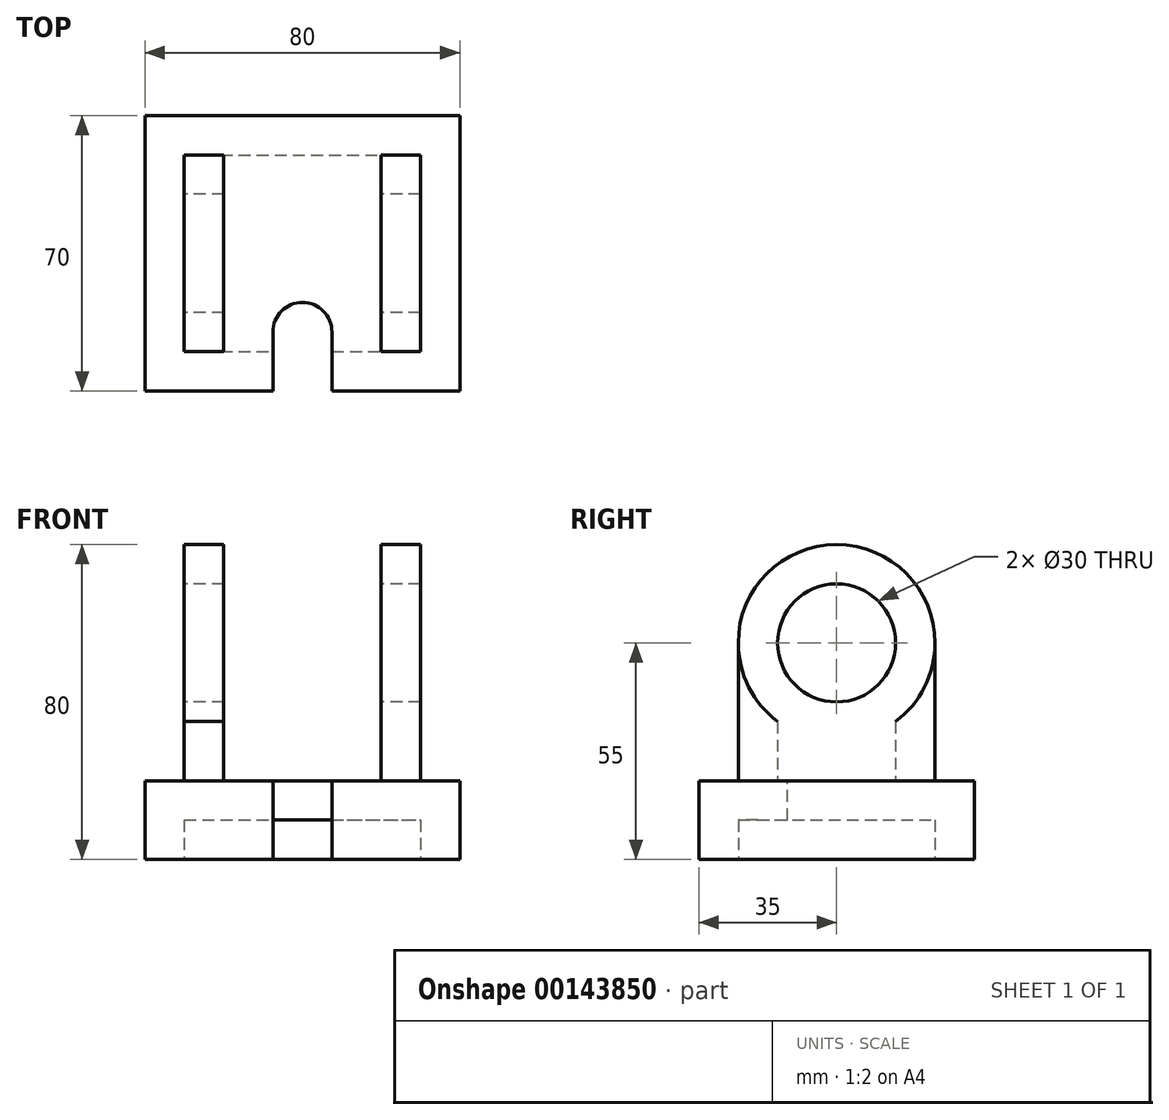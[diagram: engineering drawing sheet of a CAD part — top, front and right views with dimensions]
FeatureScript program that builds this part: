
annotation { "Feature Type Name" : "Feature", "Feature Type Description" : "" }
export const myFeature = defineFeature(function(context is Context, id is Id, definition is map)
    precondition{}
    {
        {
            var Q0;
            Q0=qCreatedBy(makeId("Top.planeOp"),FACE);
            var sketch = newSketch(context, id + "F0", { "sketchPlane" : qUnion([Q0])});
            skLineSegment(sketch, "E0.bottom", {"start": v(-40, 35) * mm, "end": v(40, 35) * mm});
            skLineSegment(sketch, "E0.top", {"start": v(-40, -35) * mm, "end": v(40, -35) * mm});
            skLineSegment(sketch, "E0.left", {"start": v(-40, 35) * mm, "end": v(-40, -35) * mm});
            skLineSegment(sketch, "E0.right", {"start": v(40, 35) * mm, "end": v(40, -35) * mm});
            skSolve(sketch);
        }
        {
            var Q0;
            Q0=makeQuery(id+"F0.imprint","IMPRINT",FACE,{"disambiguationData":[TD([[makeQuery(id+"F0.imprint","IMPRINT",EDGE,{"derivedFrom":sQuery(id+"F0.wireOp",EDGE,"E0.bottom")}),-1.0]])]});
            extrude(context, id + "F1", {"entities" : qUnion([Q0]), "depth" : 20 * mm});
        }
        {
            var Q0;
            Q0=makeQuery(id+"F1.opExtrude","CAP_FACE",FACE,{"disambiguationData":[OSD([sQuery(id+"F0.wireOp",EDGE,"E0.bottom"),sQuery(id+"F0.wireOp",EDGE,"E0.top"),sQuery(id+"F0.wireOp",EDGE,"E0.left"),sQuery(id+"F0.wireOp",EDGE,"E0.right")])],"isStart":true});
            var sketch = newSketch(context, id + "F2", { "sketchPlane" : qUnion([Q0])});
            skLineSegment(sketch, "E1.bottom", {"start": v(-30, 25) * mm, "end": v(30, 25) * mm});
            skLineSegment(sketch, "E1.top", {"start": v(-30, -25) * mm, "end": v(30, -25) * mm});
            skLineSegment(sketch, "E1.left", {"start": v(-30, 25) * mm, "end": v(-30, -25) * mm});
            skLineSegment(sketch, "E1.right", {"start": v(30, 25) * mm, "end": v(30, -25) * mm});
            skSolve(sketch);
        }
        {
            var Q0;
            Q0=makeQuery(id+"F2.imprint","IMPRINT",FACE,{"disambiguationData":[TD([[makeQuery(id+"F2.imprint","IMPRINT",EDGE,{"derivedFrom":sQuery(id+"F2.wireOp",EDGE,"E1.bottom")}),-1.0]])]});
            extrude(context, id + "F3", {"entities" : qUnion([Q0]), "operationType" : NewBodyOperationType.REMOVE, "oppositeDirection" : true, "depth" : 10 * mm});
        }
        {
            var Q0;
            Q0=makeQuery(id+"F1.opExtrude","CAP_FACE",FACE,{"disambiguationData":[OSD([sQuery(id+"F0.wireOp",EDGE,"E0.bottom"),sQuery(id+"F0.wireOp",EDGE,"E0.top"),sQuery(id+"F0.wireOp",EDGE,"E0.left"),sQuery(id+"F0.wireOp",EDGE,"E0.right")])],"isStart":false});
            var sketch = newSketch(context, id + "F4", { "sketchPlane" : qUnion([Q0])});
            skArc(sketch, "E2", {"start": v(7.5, -20) * mm, "mid": v(0, -12.5) * mm, "end": v(-7.5, -20) * mm});
            skLineSegment(sketch, "E3.top", {"start": v(-7.5, -35) * mm, "end": v(7.5, -35) * mm});
            skLineSegment(sketch, "E3.left", {"start": v(-7.5, -20) * mm, "end": v(-7.5, -35) * mm});
            skLineSegment(sketch, "E3.right", {"start": v(7.5, -20) * mm, "end": v(7.5, -35) * mm});
            skSolve(sketch);
        }
        {
            var Q0;
            Q0=makeQuery(id+"F4.imprint","IMPRINT",FACE,{"disambiguationData":[TD([[makeQuery(id+"F4.imprint","IMPRINT",EDGE,{"derivedFrom":sQuery(id+"F4.wireOp",EDGE,"E2")}),1.0]])]});
            extrude(context, id + "F5", {"entities" : qUnion([Q0]), "operationType" : NewBodyOperationType.REMOVE, "endBound" : BoundingType.UP_TO_NEXT, "oppositeDirection" : true, "depth" : 25 * mm});
        }
        {
            var Q0;
            Q0=makeQuery(id+"F1.opExtrude","CAP_FACE",FACE,{"disambiguationData":[OSD([sQuery(id+"F0.wireOp",EDGE,"E0.bottom"),sQuery(id+"F0.wireOp",EDGE,"E0.top"),sQuery(id+"F0.wireOp",EDGE,"E0.left"),sQuery(id+"F0.wireOp",EDGE,"E0.right")])],"isStart":false});
            var sketch = newSketch(context, id + "F6", { "sketchPlane" : qUnion([Q0])});
            skLineSegment(sketch, "E4.bottom", {"start": v(20, 25) * mm, "end": v(30, 25) * mm});
            skLineSegment(sketch, "E4.top", {"start": v(20, -25) * mm, "end": v(30, -25) * mm});
            skLineSegment(sketch, "E4.left", {"start": v(20, 25) * mm, "end": v(20, -25) * mm});
            skLineSegment(sketch, "E4.right", {"start": v(30, 25) * mm, "end": v(30, -25) * mm});
            skSolve(sketch);
        }
        {
            var Q0;
            Q0=makeQuery(id+"F6.imprint","IMPRINT",FACE,{"disambiguationData":[TD([[makeQuery(id+"F6.imprint","IMPRINT",EDGE,{"derivedFrom":sQuery(id+"F6.wireOp",EDGE,"E4.bottom")}),-1.0]])]});
            extrude(context, id + "F7", {"entities" : qUnion([Q0]), "operationType" : NewBodyOperationType.ADD, "depth" : 60 * mm});
        }
        {
            var Q0;
            Q0=makeQuery(id+"F7.opExtrude","CAP_EDGE",EDGE,{"disambiguationData":[OSD([sQuery(id+"F6.wireOp",EDGE,"E4.top")])],"isStart":false});
            var Q1;
            Q1=makeQuery(id+"F7.opExtrude","CAP_EDGE",EDGE,{"disambiguationData":[OSD([sQuery(id+"F6.wireOp",EDGE,"E4.bottom")])],"isStart":false});
            fillet(context, id + "F8", {"entities" : qUnion([Q0, Q1]), "radius" : 25 * mm, "tangentPropagation" : true, "allowEdgeOverflow" : false});
        }
        {
            var Q0;
            Q0=makeQuery(id+"F1.opExtrude","SWEPT_FACE",FACE,{"disambiguationData":[OSD([sQuery(id+"F0.wireOp",EDGE,"E0.left")])]});
            cPlane(context, id + "F9", {"entities" : qUnion([Q0]), "cplaneType" : CPlaneType.OFFSET, "offset" : 10 * mm, "oppositeDirection" : true, "width" : 150 * mm, "height" : 150 * mm});
        }
        {
            var Q0;
            Q0=qCreatedBy(id+"F9.planeOp",FACE);
            var sketch = newSketch(context, id + "F10", { "sketchPlane" : qUnion([Q0])});
            skArc(sketch, "E5", {"start": v(15, 35) * mm, "mid": v(0, 80) * mm, "end": v(-15, 35) * mm});
            skLineSegment(sketch, "E6.top", {"start": v(-15, 20) * mm, "end": v(15, 20) * mm});
            skLineSegment(sketch, "E6.left", {"start": v(-15, 35) * mm, "end": v(-15, 20) * mm});
            skLineSegment(sketch, "E6.right", {"start": v(15, 35) * mm, "end": v(15, 20) * mm});
            skSolve(sketch);
        }
        {
            var Q0;
            Q0=makeQuery(id+"F10.imprint","IMPRINT",FACE,{"disambiguationData":[TD([[makeQuery(id+"F10.imprint","IMPRINT",EDGE,{"derivedFrom":sQuery(id+"F10.wireOp",EDGE,"E5")}),1.0]])]});
            extrude(context, id + "F11", {"entities" : qUnion([Q0]), "operationType" : NewBodyOperationType.ADD, "oppositeDirection" : true, "depth" : 10 * mm});
        }
        {
            var Q0;
            Q0=makeQuery(id+"F11.opExtrude","CAP_FACE",FACE,{"disambiguationData":[OSD([sQuery(id+"F10.wireOp",EDGE,"E5"),sQuery(id+"F10.wireOp",EDGE,"E6.top"),sQuery(id+"F10.wireOp",EDGE,"E6.left"),sQuery(id+"F10.wireOp",EDGE,"E6.right")])],"isStart":true});
            var sketch = newSketch(context, id + "F12", { "sketchPlane" : qUnion([Q0])});
            skCircle(sketch, "E7", {"center": v(0, 55) * mm, "radius": 15 * mm});
            skSolve(sketch);
        }
        {
            var Q0;
            Q0=makeQuery(id+"F12.imprint","IMPRINT",FACE,{"disambiguationData":[TD([[makeQuery(id+"F12.imprint","IMPRINT",EDGE,{"derivedFrom":sQuery(id+"F12.wireOp",EDGE,"E7")}),1.0]])]});
            extrude(context, id + "F13", {"entities" : qUnion([Q0]), "operationType" : NewBodyOperationType.REMOVE, "endBound" : BoundingType.THROUGH_ALL, "oppositeDirection" : true, "depth" : 25 * mm});
        }
    });
